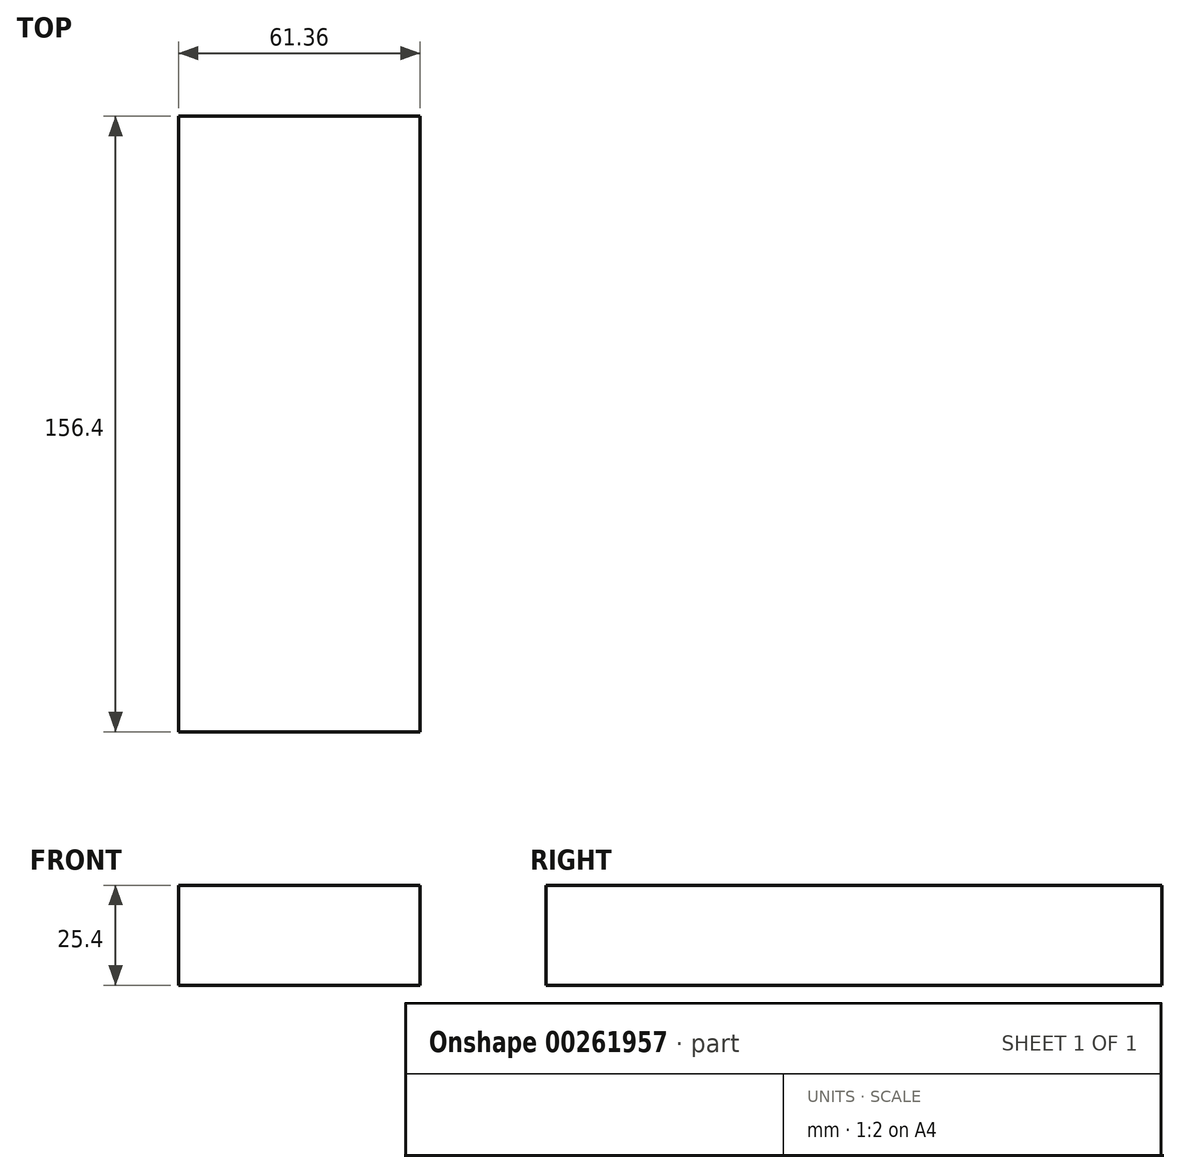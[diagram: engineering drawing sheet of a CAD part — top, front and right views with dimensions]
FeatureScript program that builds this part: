
annotation { "Feature Type Name" : "Feature", "Feature Type Description" : "" }
export const myFeature = defineFeature(function(context is Context, id is Id, definition is map)
    precondition{}
    {
        {
            var Q0;
            Q0=qCreatedBy(makeId("Top.planeOp"),FACE);
            var sketch = newSketch(context, id + "F0", { "sketchPlane" : qUnion([Q0])});
            skLineSegment(sketch, "E0.bottom", {"start": v(-130.86, 75.34) * mm, "end": v(-69.5, 75.34) * mm});
            skLineSegment(sketch, "E0.top", {"start": v(-130.86, -81.06) * mm, "end": v(-69.5, -81.06) * mm});
            skLineSegment(sketch, "E0.left", {"start": v(-130.86, 75.34) * mm, "end": v(-130.86, -81.06) * mm});
            skLineSegment(sketch, "E0.right", {"start": v(-69.5, 75.34) * mm, "end": v(-69.5, -81.06) * mm});
            skSolve(sketch);
        }
        {
            var Q0;
            Q0=makeQuery(id+"F0.imprint","IMPRINT",FACE,{"disambiguationData":[TD([[makeQuery(id+"F0.imprint","IMPRINT",EDGE,{"derivedFrom":sQuery(id+"F0.wireOp",EDGE,"E0.bottom")}),-1.0]])]});
            extrude(context, id + "F1", {"entities" : qUnion([Q0]), "depth" : 25.4 * mm});
        }
    });
